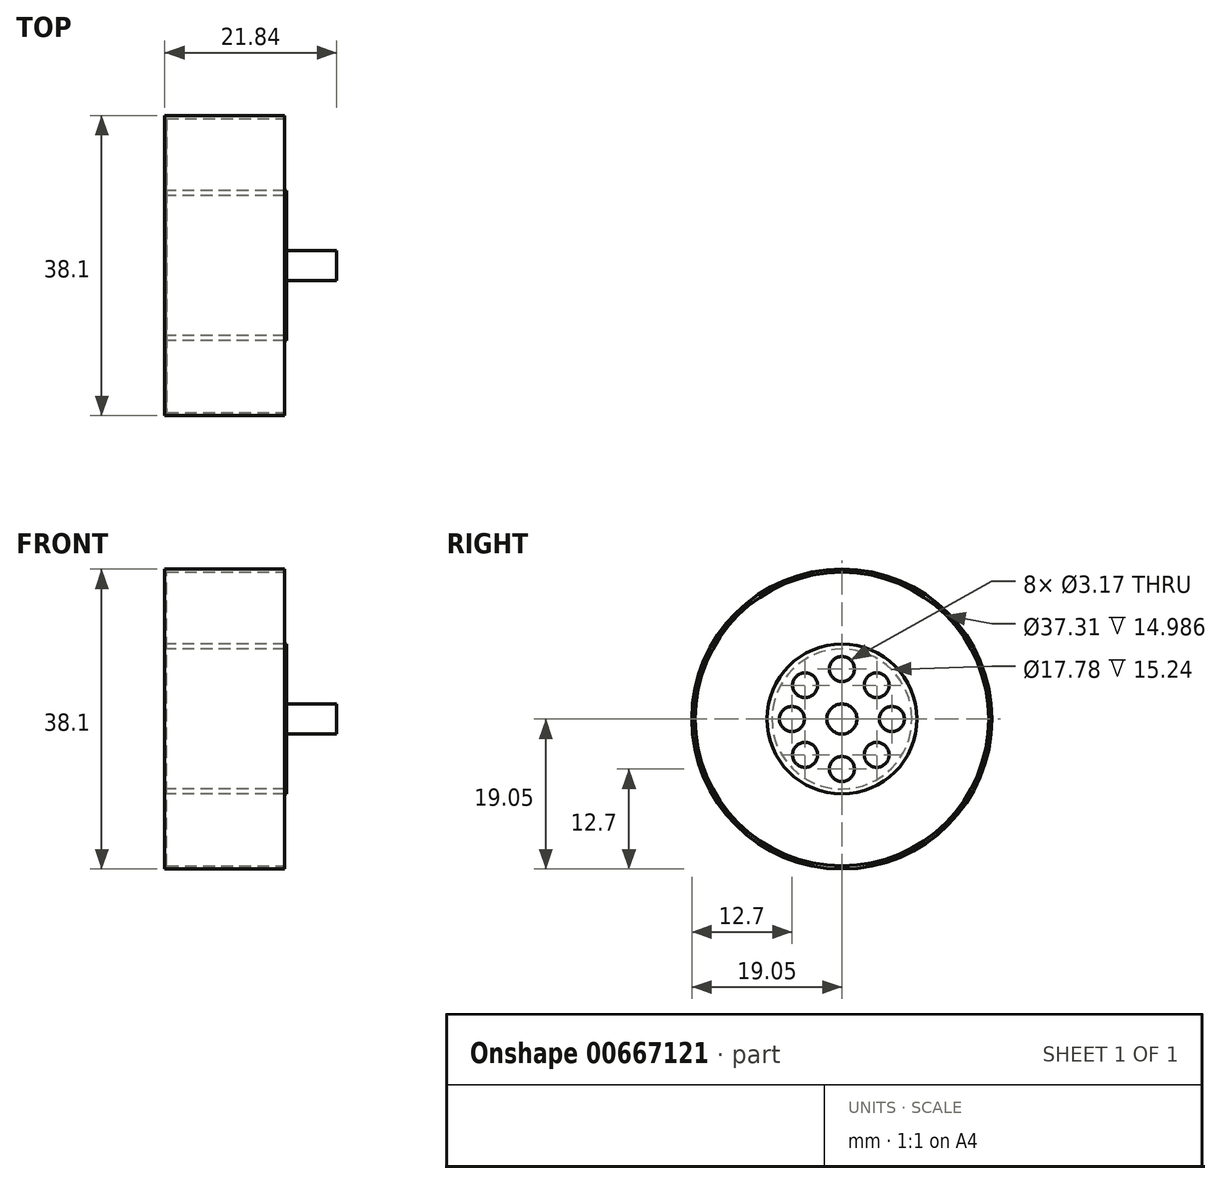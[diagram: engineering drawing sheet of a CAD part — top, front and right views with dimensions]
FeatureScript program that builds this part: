
annotation { "Feature Type Name" : "Feature", "Feature Type Description" : "" }
export const myFeature = defineFeature(function(context is Context, id is Id, definition is map)
    precondition{}
    {
        {
            var Q0;
            Q0=qCreatedBy(makeId("Right.planeOp"),FACE);
            var sketch = newSketch(context, id + "F0", { "sketchPlane" : qUnion([Q0])});
            skCircle(sketch, "E0", {"center": v(0, 0) * mm, "radius": 19.05 * mm});
            skSolve(sketch);
        }
        {
            var Q0;
            Q0 = qSketchRegion(id + "F0", true);
            extrude(context, id + "F1", {"entities" : qUnion([Q0]), "depth" : 15.24 * mm, "offsetDistance" : 25.4 * mm});
        }
        {
            var Q0;
            Q0=makeQuery(id+"F1.opExtrude","CAP_FACE",FACE,{"disambiguationData":[OSD([sQuery(id+"F0.wireOp",EDGE,"E0")])],"isStart":false});
            var sketch = newSketch(context, id + "F2", { "sketchPlane" : qUnion([Q0])});
            skCircle(sketch, "E1", {"center": v(0, 0) * mm, "radius": 18.65 * mm});
            skSolve(sketch);
        }
        {
            var Q0;
            Q0 = qSketchRegion(id + "F2", true);
            extrude(context, id + "F3", {"entities" : qUnion([Q0]), "operationType" : NewBodyOperationType.REMOVE, "oppositeDirection" : true, "depth" : 15 * mm, "offsetDistance" : 25.4 * mm});
        }
        {
            var Q0;
            Q0=makeQuery(id+"F3.boolean.opBoolean","COPY",FACE,{"derivedFrom":makeQuery(id+"F3.opExtrude","CAP_FACE",FACE,{"disambiguationData":[OSD([sQuery(id+"F2.wireOp",EDGE,"E1")])],"isStart":false})});
            var sketch = newSketch(context, id + "F4", { "sketchPlane" : qUnion([Q0])});
            skCircle(sketch, "E2", {"center": v(0, 0) * mm, "radius": 9.53 * mm});
            skSolve(sketch);
        }
        {
            var Q0;
            Q0 = qSketchRegion(id + "F4", true);
            var Q1;
            Q1 = qSketchRegion(id + "F6", true);
            extrude(context, id + "F5", {"entities" : qUnion([Q0, Q1]), "operationType" : NewBodyOperationType.ADD, "depth" : 15.24 * mm, "offsetDistance" : 25.4 * mm});
        }
        {
            var Q0;
            Q0=makeQuery(id+"F5.opExtrude","CAP_FACE",FACE,{"disambiguationData":[OSD([sQuery(id+"F4.wireOp",EDGE,"E2")])],"isStart":false});
            var sketch = newSketch(context, id + "F6", { "sketchPlane" : qUnion([Q0])});
            skCircle(sketch, "E3", {"center": v(0, 0) * mm, "radius": 9.4 * mm});
            skSolve(sketch);
        }
        {
            var Q0;
            Q0=makeQuery(id+"F6.imprint","IMPRINT",FACE,{"disambiguationData":[TD([[makeQuery(id+"F6.imprint","IMPRINT",EDGE,{"derivedFrom":sQuery(id+"F6.wireOp",EDGE,"E3")}),1.0]])]});
            var sketch = newSketch(context, id + "F7", { "sketchPlane" : qUnion([Q0])});
            skLineSegment(sketch, "E4", {"start": v(0, 0) * mm, "end": v(0, 6.35) * mm});
            skLineSegment(sketch, "E5", {"start": v(0, 0) * mm, "end": v(6.35, 0) * mm});
            skLineSegment(sketch, "E6", {"start": v(0, 0) * mm, "end": v(0, -6.35) * mm});
            skLineSegment(sketch, "E7", {"start": v(0, 0) * mm, "end": v(-6.35, 0) * mm});
            skLineSegment(sketch, "E8", {"start": v(0, 0) * mm, "end": v(4.42, 4.3) * mm});
            skLineSegment(sketch, "E9", {"start": v(4.42, 4.3) * mm, "end": v(0, 0) * mm});
            skLineSegment(sketch, "E10", {"start": v(0, 0) * mm, "end": v(4.42, -4.55) * mm});
            skLineSegment(sketch, "E11", {"start": v(4.42, -4.55) * mm, "end": v(0, 0) * mm});
            skLineSegment(sketch, "E12", {"start": v(0, 0) * mm, "end": v(-4.68, -4.55) * mm});
            skLineSegment(sketch, "E13", {"start": v(-4.68, -4.55) * mm, "end": v(0, 0) * mm});
            skLineSegment(sketch, "E14", {"start": v(0, 0) * mm, "end": v(-4.68, 4.3) * mm});
            skLineSegment(sketch, "E15", {"start": v(-4.68, 4.3) * mm, "end": v(0, 0) * mm});
            skCircle(sketch, "E16", {"center": v(0, 6.35) * mm, "radius": 1.59 * mm});
            skCircle(sketch, "E17", {"center": v(4.42, 4.3) * mm, "radius": 1.59 * mm});
            skCircle(sketch, "E18", {"center": v(6.35, 0) * mm, "radius": 1.59 * mm});
            skCircle(sketch, "E19", {"center": v(4.42, -4.55) * mm, "radius": 1.59 * mm});
            skCircle(sketch, "E20", {"center": v(0, -6.35) * mm, "radius": 1.59 * mm});
            skCircle(sketch, "E21", {"center": v(-4.68, -4.55) * mm, "radius": 1.59 * mm});
            skCircle(sketch, "E22", {"center": v(-6.35, 0) * mm, "radius": 1.59 * mm});
            skCircle(sketch, "E23", {"center": v(-4.68, 4.3) * mm, "radius": 1.59 * mm});
            skSolve(sketch);
        }
        {
            var Q0;
            Q0 = qSketchRegion(id + "F7", true);
            extrude(context, id + "F8", {"entities" : qUnion([Q0]), "operationType" : NewBodyOperationType.REMOVE, "oppositeDirection" : true, "depth" : 2.54 * mm, "offsetDistance" : 25.4 * mm});
        }
        {
            var Q0;
            Q0=makeQuery(id+"F1.opExtrude","CAP_FACE",FACE,{"disambiguationData":[OSD([sQuery(id+"F0.wireOp",EDGE,"E0")])],"isStart":true});
            var sketch = newSketch(context, id + "F9", { "sketchPlane" : qUnion([Q0])});
            skCircle(sketch, "E24", {"center": v(0, 0) * mm, "radius": 8.9 * mm});
            skSolve(sketch);
        }
        {
            var Q0;
            Q0 = qSketchRegion(id + "F9", true);
            extrude(context, id + "F10", {"entities" : qUnion([Q0]), "operationType" : NewBodyOperationType.REMOVE, "oppositeDirection" : true, "depth" : 15.24 * mm, "offsetDistance" : 25.4 * mm});
        }
        {
            var Q0;
            Q0=makeQuery(id+"F6.imprint","IMPRINT",FACE,{"disambiguationData":[TD([[makeQuery(id+"F6.imprint","IMPRINT",EDGE,{"derivedFrom":sQuery(id+"F6.wireOp",EDGE,"E3")}),1.0]])]});
            var sketch = newSketch(context, id + "F11", { "sketchPlane" : qUnion([Q0])});
            skCircle(sketch, "E25", {"center": v(0, 0) * mm, "radius": 1.9 * mm});
            skSolve(sketch);
        }
        {
            var Q0;
            Q0 = qSketchRegion(id + "F11", true);
            extrude(context, id + "F12", {"entities" : qUnion([Q0]), "operationType" : NewBodyOperationType.ADD, "depth" : 6.35 * mm, "offsetDistance" : 25.4 * mm});
        }
    });
